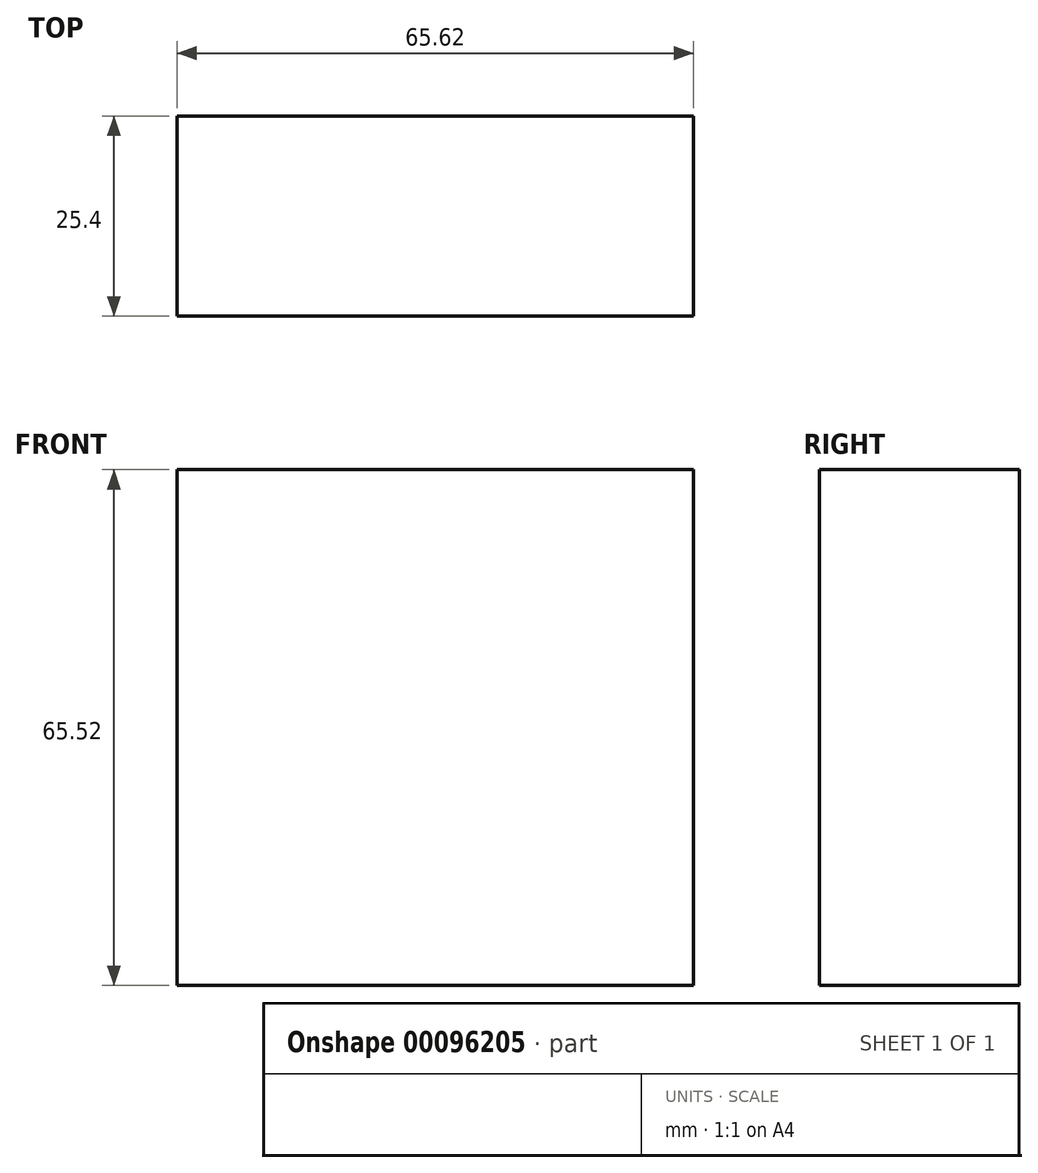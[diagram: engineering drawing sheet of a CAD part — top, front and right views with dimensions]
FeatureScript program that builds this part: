
annotation { "Feature Type Name" : "Feature", "Feature Type Description" : "" }
export const myFeature = defineFeature(function(context is Context, id is Id, definition is map)
    precondition{}
    {
        {
            var Q0;
            Q0=qCreatedBy(makeId("Front.planeOp"),FACE);
            var sketch = newSketch(context, id + "F0", { "sketchPlane" : qUnion([Q0])});
            skLineSegment(sketch, "E0.bottom", {"start": v(32.81, 32.76) * mm, "end": v(-32.81, 32.76) * mm});
            skLineSegment(sketch, "E0.top", {"start": v(32.81, -32.76) * mm, "end": v(-32.81, -32.76) * mm});
            skLineSegment(sketch, "E0.left", {"start": v(32.81, 32.76) * mm, "end": v(32.81, -32.76) * mm});
            skLineSegment(sketch, "E0.right", {"start": v(-32.81, 32.76) * mm, "end": v(-32.81, -32.76) * mm});
            skPoint(sketch, "E0.middle", {"position": v(0, 0) * mm});
            skSolve(sketch);
        }
        {
            var Q0;
            Q0=makeQuery(id+"F0.imprint","IMPRINT",FACE,{"disambiguationData":[TD([[makeQuery(id+"F0.imprint","IMPRINT",EDGE,{"derivedFrom":sQuery(id+"F0.wireOp",EDGE,"E0.bottom")}),1.0]])]});
            extrude(context, id + "F1", {"entities" : qUnion([Q0]), "depth" : 25.4 * mm});
        }
    });
